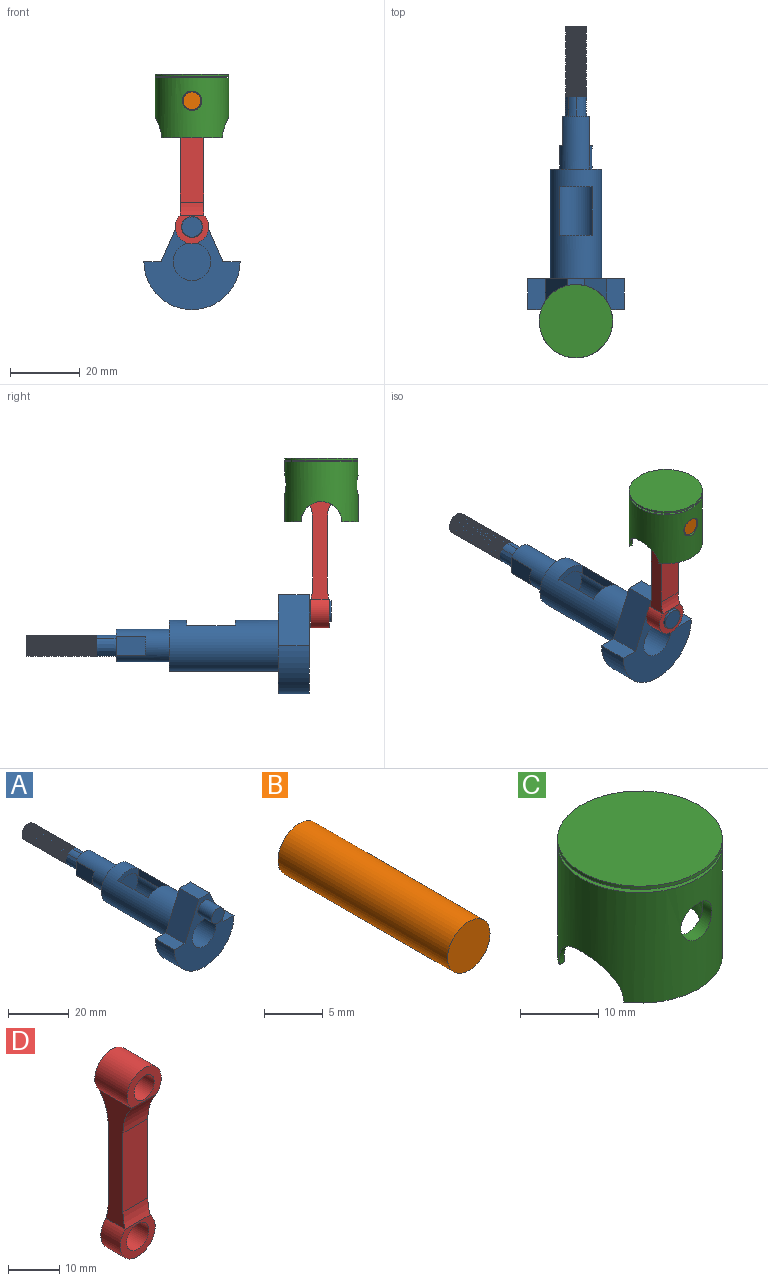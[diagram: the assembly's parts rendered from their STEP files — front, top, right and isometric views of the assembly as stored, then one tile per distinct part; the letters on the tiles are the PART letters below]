
ASSEMBLY  parts=4 mates=3
PART A: 32 faces, bbox 27.8x88.3x28.6 mm
  f0: cylinder r=3.05mm len=25.91mm, axis (0,1,0), area 21.5mm2, adj f1,f3,f4,f5,f7
  f1: plane 5.94x5.92mm, normal (0,1,0), area 26.3mm2, adj f0,f2,f3,f4
  f2: bspline ~20.7x6.4mm, area 98.6mm2, adj f1,f3,f4,f6
  f3: bspline ~20.73x7.04mm, area 232.2mm2, adj f0,f1,f2,f6
  f4: bspline ~20.65x7.04mm, area 232.3mm2, adj f0,f1,f2,f6
  f5: extruded ~6.09x6.09mm, area 93.8mm2, adj f0,f6,f7
  f6: plane 6.25x6.25mm, normal (0,1,0), area 2.9mm2, adj f2,f3,f4,f5
  f7: plane 9.4x7.62mm, normal (0,1,0), area 33.5mm2, adj f0,f5,f8,f9,f10
  f8: cylinder r=4.7mm len=15.24mm, axis (0,1,0), area 311.1mm2, adj f7,f9,f10,f11,f12,f14
  f9: plane 8.38x5.5mm, normal (-1,0,0), area 46.1mm2, adj f7,f8,f11
  f10: plane 8.38x5.5mm, normal (1,0,0), area 46.1mm2, adj f7,f8,f13
  f11: plane 5.5x0.89mm, normal (0,1,0), area 3.3mm2, adj f8,f9
  f12: extruded ~6.86x5.5mm, area 40.3mm2, adj f8,f13,f14
  f13: plane 5.5x0.89mm, normal (0,1,0), area 3.3mm2, adj f10,f12
  f14: plane 14.73x14.73mm, normal (0,1,0), area 101.1mm2, adj f8,f12,f19
  f15: plane 13.97x2.89mm, normal (-1,0,0), area 40.4mm2, adj f16,f18,f19,f20
  f16: plane 9.4x4.58mm, normal (0,-1,0), area 20.2mm2, adj f15,f17,f19,f20
  f17: plane 13.97x2.89mm, normal (1,0,0), area 40.4mm2, adj f16,f18,f19,f20
  f18: plane 9.4x4.58mm, normal (0,1,0), area 20.2mm2, adj f15,f17,f19,f20
  f19: cylinder r=7.37mm len=31.5mm, axis (0,-1,0), area 1315.3mm2, adj f14,f15,f16,f17,f18,f29
  f20: cylinder r=5.46mm len=36.32mm, axis (0,-1,0), area 1088.2mm2, adj f15,f16,f17,f18,f21,f28
  f21: plane 10.92x10.92mm, normal (0,-1,0), area 93.7mm2, adj f20
  f22: plane 8.89x4.95mm, normal (0,0,1), area 44mm2, adj f23,f27,f28,f29
  f23: plane 14.66x8.89mm, normal (0.92,0,0.4), area 142mm2, adj f22,f24,f28,f29
  f24: plane 8.89x5.08mm, normal (0,0,1), area 45.2mm2, adj f23,f25,f28,f29
  f25: plane 14.66x8.89mm, normal (-0.92,0,0.4), area 142mm2, adj f24,f26,f28,f29
  f26: plane 8.89x4.95mm, normal (0,0,1), area 44mm2, adj f25,f27,f28,f29
  f27: cylinder r=13.84mm len=27.69mm, axis (0,1,0), area 386.6mm2, adj f22,f26,f28,f29
  f28: plane 28.5x27.69mm, normal (0,-1,0), area 348mm2, adj f20,f22,f23,f24,f25,f26,f27,f30
  f29: plane 28.5x27.69mm, normal (0,1,0), area 298.1mm2, adj f19,f22,f23,f24,f25,f26,f27
  f30: cylinder r=2.92mm len=6.35mm, axis (0,1,0), area 116.5mm2, adj f28,f31
  f31: plane 5.84x5.84mm, normal (0,-1,0), area 26.8mm2, adj f30
PART B: 3 faces, bbox 5.1x20.3x5.1 mm
  f0: plane 5.08x5.08mm, normal (0,-1,0), area 20.3mm2, adj f1
  f1: cylinder r=2.54mm len=20.35mm, axis (0,-1,0), area 324.7mm2, adj f0,f2
  f2: plane 5.08x5.08mm, normal (0,1,0), area 20.3mm2, adj f1
PART C: 18 faces, bbox 21.1x21.1x18.3 mm
  f0: extruded ~18.12x12.68mm, area 406.8mm2, adj f1,f3,f12,f14,f15,f17
  f1: plane 5.48x4.03mm, normal (0,1,0), area 12.8mm2, adj f0,f3,f17
  f2: cylinder r=5.84mm len=11.68mm, axis (-1,0,0), area 15.4mm2, adj f4,f9,f13,f16
  f3: cylinder r=2.79mm len=5.59mm, axis (0,-1,0), area 30.8mm2, adj f0,f1,f13,f14
  f4: plane 17.55x4.7mm, normal (0,0,-1), area 14.8mm2, adj f2,f11,f13,f16
  f5: cylinder r=10.54mm len=21.08mm, axis (0,0,-1), area 33.6mm2, adj f6,f7
  f6: plane 21.08x21.08mm, normal (0,0,1), area 349.1mm2, adj f5
  f7: plane 21.08x21.08mm, normal (0,0,-1), area 79mm2, adj f5,f8
  f8: cylinder r=9.27mm len=18.54mm, axis (0,0,1), area 29.6mm2, adj f7,f10
  f9: plane 17.55x4.7mm, normal (0,0,-1), area 14.8mm2, adj f2,f11,f13,f16
  f10: plane 21.08x21.08mm, normal (0,0,1), area 79mm2, adj f8,f13
  f11: cylinder r=5.84mm len=11.68mm, axis (-1,0,0), area 15.4mm2, adj f4,f9,f13,f16
  f12: cylinder r=2.79mm len=5.59mm, axis (0,-1,0), area 22.9mm2, adj f0,f13
  f13: cylinder r=10.54mm len=21.08mm, axis (0,0,-1), area 982.5mm2, adj f2,f3,f4,f9,f10,f11,f12
  f14: plane 5.48x4.61mm, normal (0,1,0), area 16mm2, adj f0,f3,f15
  f15: plane 18.12x12.7mm, normal (0,0,-1), area 186.6mm2, adj f0,f14
  f16: cylinder r=9.78mm len=19.56mm, axis (0,0,-1), area 261.8mm2, adj f2,f4,f9,f11,f17
  f17: plane 19.56x19.56mm, normal (0,0,-1), area 113.9mm2, adj f0,f1,f16
PART D: 16 faces, bbox 9.7x8.9x45.8 mm
  f0: cylinder r=3.05mm len=6.1mm, axis (0,-1,0), area 102.1mm2, adj f3,f6
  f1: plane 9.4x7.91mm, normal (0,1,0), area 37.8mm2, adj f7,f8,f14
  f2: plane 18.86x6.86mm, normal (0,1,0), area 129.3mm2, adj f9,f11,f13,f14
  f3: plane 9.65x8.22mm, normal (0,1,0), area 37.2mm2, adj f0,f10,f13
  f4: plane 18.86x6.86mm, normal (0,-1,0), area 129.3mm2, adj f9,f11,f12,f15
  f5: plane 9.4x7.91mm, normal (0,-1,0), area 37.8mm2, adj f7,f8,f15
  f6: plane 9.65x8.22mm, normal (0,-1,0), area 37.2mm2, adj f0,f10,f12
  f7: cylinder r=2.79mm len=8.89mm, axis (0,-1,0), area 156.1mm2, adj f1,f5
  f8: cylinder r=4.7mm len=9.4mm, axis (0,-1,0), area 194.1mm2, adj f1,f5,f9,f11
  f9: plane 29.71x8.89mm, normal (-1,0,0), area 133.2mm2, adj f2,f4,f8,f10,f12,f13,f14,f15
  f10: cylinder r=4.83mm len=9.65mm, axis (0,-1,0), area 121mm2, adj f3,f6,f9,f11
  f11: plane 29.71x8.89mm, normal (1,0,0), area 133.2mm2, adj f2,f4,f8,f10,f12,f13,f14,f15
  f12: cylinder r=11.59mm len=6.86mm, axis (1,0,0), area 26.4mm2, adj f4,f6,f9,f11
  f13: cylinder r=11.59mm len=6.86mm, axis (1,0,0), area 26.4mm2, adj f2,f3,f9,f11
  f14: cylinder r=11.59mm len=7.08mm, axis (-1,0,0), area 52.2mm2, adj f1,f2,f9,f11
  f15: cylinder r=11.59mm len=7.08mm, axis (-1,0,0), area 52.2mm2, adj f4,f5,f9,f11
PLACE A t=(25.12,18.95,-5.43)mm
PLACE B t=(25.12,-65.66,47.96)mm
PLACE C t=(25.12,-66.03,47.96)mm
PLACE D t=(25.12,-66.51,47.96)mm
MATE cylindrical D.f7 <-> B.f1  axis (0,-1,0) through (25.12,-65.63,40.85)mm
MATE fastened B.f1 <-> C.f3  axis (0,-1,0) through (25.12,-76.2,40.85)mm
MATE revolute D.f0 <-> A.f30  axis (0,-1,0) through (25.12,-68.29,4.52)mm
